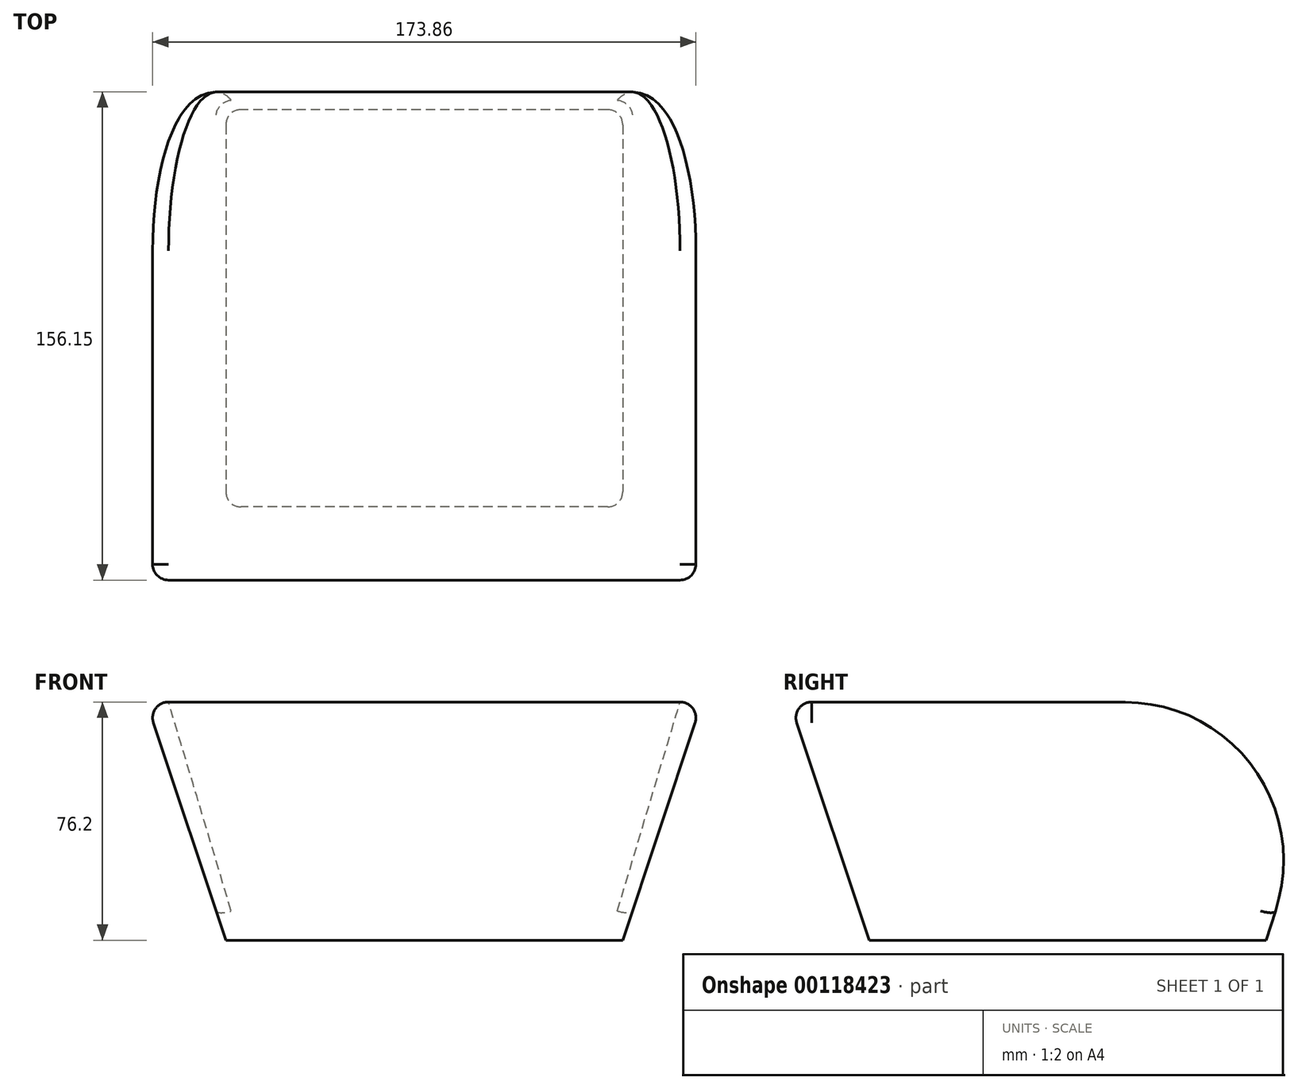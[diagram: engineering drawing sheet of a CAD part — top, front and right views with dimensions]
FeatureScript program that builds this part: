
annotation { "Feature Type Name" : "Feature", "Feature Type Description" : "" }
export const myFeature = defineFeature(function(context is Context, id is Id, definition is map)
    precondition{}
    {
        {
            var Q0;
            Q0=qCreatedBy(makeId("Top.planeOp"),FACE);
            var sketch = newSketch(context, id + "F0", { "sketchPlane" : qUnion([Q0])});
            skLineSegment(sketch, "E0.bottom", {"start": v(63.5, 63.5) * mm, "end": v(-63.5, 63.5) * mm});
            skLineSegment(sketch, "E0.top", {"start": v(63.5, -63.5) * mm, "end": v(-63.5, -63.5) * mm});
            skLineSegment(sketch, "E0.left", {"start": v(63.5, 63.5) * mm, "end": v(63.5, -63.5) * mm});
            skLineSegment(sketch, "E0.right", {"start": v(-63.5, 63.5) * mm, "end": v(-63.5, -63.5) * mm});
            skPoint(sketch, "E0.middle", {"position": v(0, 0) * mm});
            skSolve(sketch);
        }
        {
            var Q0;
            Q0=qCreatedBy(makeId("Top.planeOp"),FACE);
            cPlane(context, id + "F1", {"entities" : qUnion([Q0]), "cplaneType" : CPlaneType.OFFSET, "offset" : 76.2 * mm, "width" : 152.4 * mm, "height" : 152.4 * mm});
        }
        {
            var Q0;
            Q0=qCreatedBy(id+"F1.planeOp",FACE);
            var sketch = newSketch(context, id + "F2", { "sketchPlane" : qUnion([Q0])});
            skLineSegment(sketch, "E1.bottom", {"start": v(88.9, -88.9) * mm, "end": v(-88.9, -88.9) * mm});
            skLineSegment(sketch, "E1.top", {"start": v(88.9, 88.9) * mm, "end": v(-88.9, 88.9) * mm});
            skLineSegment(sketch, "E1.left", {"start": v(88.9, -88.9) * mm, "end": v(88.9, 88.9) * mm});
            skLineSegment(sketch, "E1.right", {"start": v(-88.9, -88.9) * mm, "end": v(-88.9, 88.9) * mm});
            skPoint(sketch, "E1.middle", {"position": v(0, 0) * mm});
            skSolve(sketch);
        }
        {
            var Q0;
            Q0=makeQuery(id+"F0.imprint","IMPRINT",FACE,{"disambiguationData":[TD([[makeQuery(id+"F0.imprint","IMPRINT",EDGE,{"derivedFrom":sQuery(id+"F0.wireOp",EDGE,"E0.bottom")}),1.0]])]});
            var Q1;
            Q1=makeQuery(id+"F2.imprint","IMPRINT",FACE,{"disambiguationData":[TD([[makeQuery(id+"F2.imprint","IMPRINT",EDGE,{"derivedFrom":sQuery(id+"F2.wireOp",EDGE,"E1.bottom")}),-1.0]])]});
            loft(context, id + "F3", {"sheetProfilesArray" : [{ "sheetProfileEntities" : qUnion([Q0]) }, { "sheetProfileEntities" : qUnion([Q1]) }]});
        }
        {
            var Q0;
            Q0=makeQuery(id+"F3.opLoft","MID_CAP_EDGE",EDGE,{"disambiguationData":[OSD([sQuery(id+"F2.wireOp",EDGE,"E1.top"),sQuery(id+"F2.wireOp",EDGE,"E1.left"),sQuery(id+"F2.wireOp",EDGE,"E1.right")])],"capPos":1.0});
            fillet(context, id + "F4", {"entities" : qUnion([Q0]), "radius" : 50.8 * mm, "tangentPropagation" : true, "allowEdgeOverflow" : false});
        }
        {
            var Q0;
            Q0=makeQuery(id+"F3.opLoft","MID_CAP_EDGE",EDGE,{"disambiguationData":[OSD([sQuery(id+"F2.wireOp",EDGE,"E1.bottom"),sQuery(id+"F2.wireOp",EDGE,"E1.top"),sQuery(id+"F2.wireOp",EDGE,"E1.left")])],"capPos":1.0});
            var Q1;
            {var subQ0=sQuery(id+"F2.wireOp",EDGE,"E1.left");var subQ1=sQuery(id+"F2.wireOp",EDGE,"E1.top");Q1=makeQuery(id+"F4.opFillet","BLEND_EDGE",EDGE,{"blendedFrom":[makeQuery(id+"F3.opLoft","MID_CAP_EDGE",EDGE,{"disambiguationData":[OSD([subQ1,subQ0,sQuery(id+"F2.wireOp",EDGE,"E1.right")])],"capPos":1.0}),makeQuery(id+"F3.opLoft","SWEPT_FACE",FACE,{"disambiguationData":[OSD([sQuery(id+"F0.wireOp",EDGE,"E0.bottom"),sQuery(id+"F0.wireOp",EDGE,"E0.top"),sQuery(id+"F0.wireOp",EDGE,"E0.left"),sQuery(id+"F2.wireOp",EDGE,"E1.bottom"),subQ1,subQ0])]})],"blendedInto":[makeQuery(id+"F3.opLoft","SWEPT_FACE",FACE,{"disambiguationData":[OSD([sQuery(id+"F0.wireOp",EDGE,"E0.bottom"),sQuery(id+"F0.wireOp",EDGE,"E0.top"),sQuery(id+"F0.wireOp",EDGE,"E0.left"),sQuery(id+"F2.wireOp",EDGE,"E1.bottom"),subQ1,subQ0])]})]});}
            var Q2;
            Q2=makeQuery(id+"F3.opLoft","SWEPT_EDGE",EDGE,{"disambiguationData":[OSD([sQuery(id+"F0.wireOp",EDGE,"E0.bottom"),sQuery(id+"F0.wireOp",EDGE,"E0.left"),sQuery(id+"F2.wireOp",EDGE,"E1.top"),sQuery(id+"F2.wireOp",EDGE,"E1.left")])]});
            var Q3;
            Q3=makeQuery(id+"F3.opLoft","MID_CAP_EDGE",EDGE,{"disambiguationData":[OSD([sQuery(id+"F2.wireOp",EDGE,"E1.bottom"),sQuery(id+"F2.wireOp",EDGE,"E1.top"),sQuery(id+"F2.wireOp",EDGE,"E1.right")])],"capPos":1.0});
            var Q4;
            {var subQ0=sQuery(id+"F2.wireOp",EDGE,"E1.right");var subQ1=sQuery(id+"F2.wireOp",EDGE,"E1.top");Q4=makeQuery(id+"F4.opFillet","BLEND_EDGE",EDGE,{"blendedFrom":[makeQuery(id+"F3.opLoft","MID_CAP_EDGE",EDGE,{"disambiguationData":[OSD([subQ1,sQuery(id+"F2.wireOp",EDGE,"E1.left"),subQ0])],"capPos":1.0}),makeQuery(id+"F3.opLoft","SWEPT_FACE",FACE,{"disambiguationData":[OSD([sQuery(id+"F0.wireOp",EDGE,"E0.bottom"),sQuery(id+"F0.wireOp",EDGE,"E0.top"),sQuery(id+"F0.wireOp",EDGE,"E0.right"),sQuery(id+"F2.wireOp",EDGE,"E1.bottom"),subQ1,subQ0])]})],"blendedInto":[makeQuery(id+"F3.opLoft","SWEPT_FACE",FACE,{"disambiguationData":[OSD([sQuery(id+"F0.wireOp",EDGE,"E0.bottom"),sQuery(id+"F0.wireOp",EDGE,"E0.top"),sQuery(id+"F0.wireOp",EDGE,"E0.right"),sQuery(id+"F2.wireOp",EDGE,"E1.bottom"),subQ1,subQ0])]})]});}
            var Q5;
            Q5=makeQuery(id+"F3.opLoft","SWEPT_EDGE",EDGE,{"disambiguationData":[OSD([sQuery(id+"F0.wireOp",EDGE,"E0.bottom"),sQuery(id+"F0.wireOp",EDGE,"E0.right"),sQuery(id+"F2.wireOp",EDGE,"E1.top"),sQuery(id+"F2.wireOp",EDGE,"E1.right")])]});
            fillet(context, id + "F5", {"entities" : qUnion([Q0, Q1, Q2, Q3, Q4, Q5]), "radius" : 5.08 * mm, "tangentPropagation" : true, "allowEdgeOverflow" : false});
        }
        {
            var Q0;
            Q0=makeQuery(id+"F3.opLoft","MID_CAP_EDGE",EDGE,{"disambiguationData":[OSD([sQuery(id+"F2.wireOp",EDGE,"E1.bottom"),sQuery(id+"F2.wireOp",EDGE,"E1.left"),sQuery(id+"F2.wireOp",EDGE,"E1.right")])],"capPos":1.0});
            fillet(context, id + "F6", {"entities" : qUnion([Q0]), "radius" : 5.08 * mm, "tangentPropagation" : true, "allowEdgeOverflow" : false});
        }
    });
